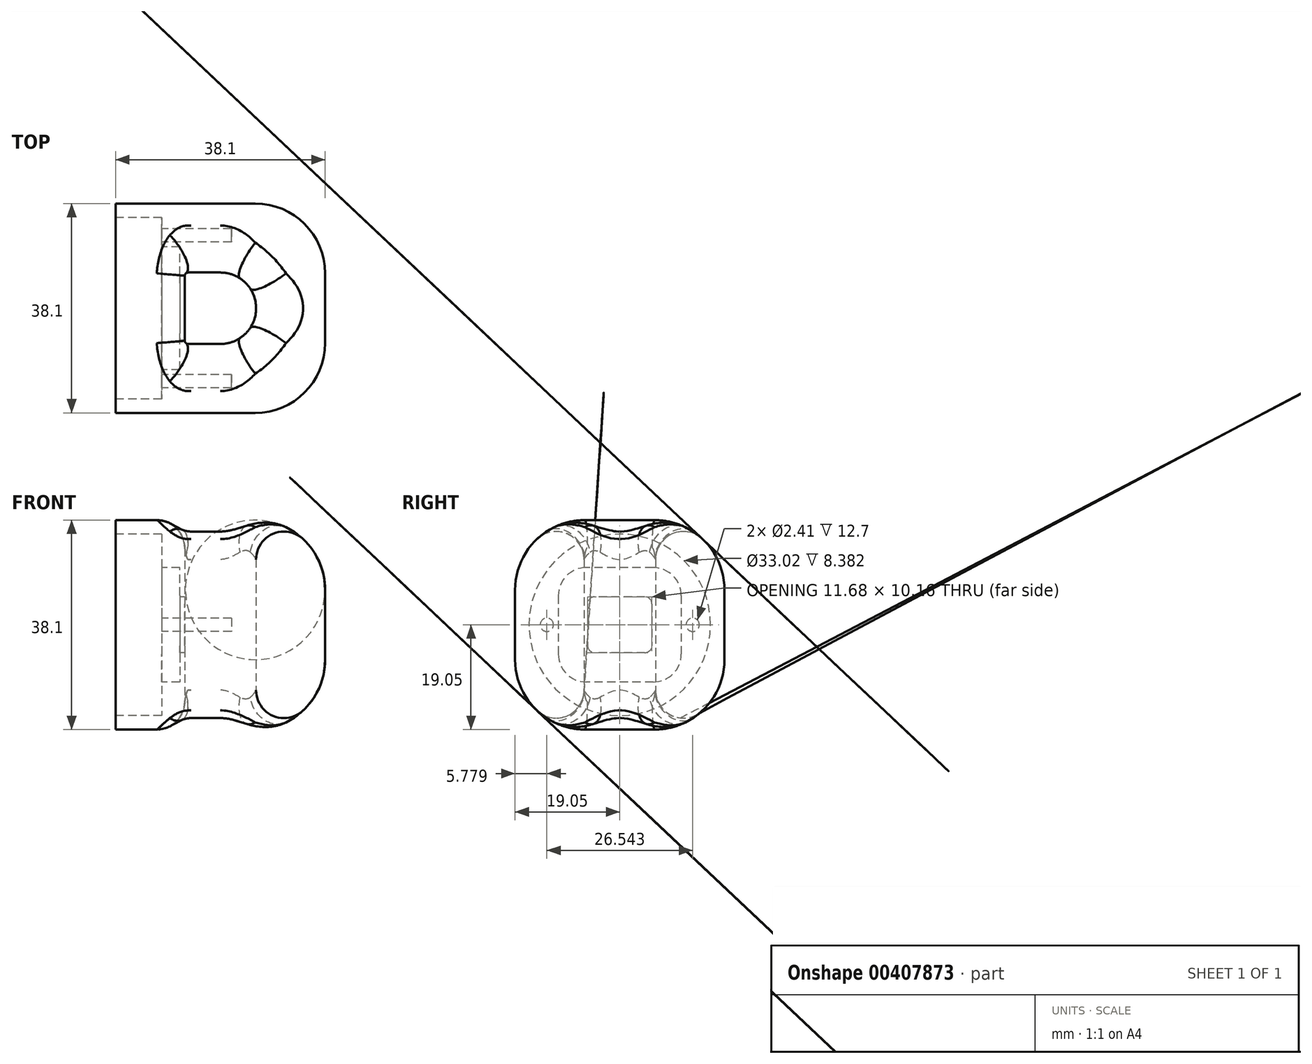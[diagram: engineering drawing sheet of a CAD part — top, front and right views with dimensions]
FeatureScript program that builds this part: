
annotation { "Feature Type Name" : "Feature", "Feature Type Description" : "" }
export const myFeature = defineFeature(function(context is Context, id is Id, definition is map)
    precondition{}
    {
        {
            var Q0;
            Q0=qCreatedBy(makeId("Top.planeOp"),FACE);
            var sketch = newSketch(context, id + "F0", { "sketchPlane" : qUnion([Q0])});
            skLineSegment(sketch, "E0.bottom", {"start": v(19.05, 19.05) * mm, "end": v(-19.05, 19.05) * mm});
            skLineSegment(sketch, "E0.top", {"start": v(19.05, -19.05) * mm, "end": v(-19.05, -19.05) * mm});
            skLineSegment(sketch, "E0.left", {"start": v(19.05, 19.05) * mm, "end": v(19.05, -19.05) * mm});
            skLineSegment(sketch, "E0.right", {"start": v(-19.05, 19.05) * mm, "end": v(-19.05, -19.05) * mm});
            skPoint(sketch, "E0.middle", {"position": v(0, 0) * mm});
            skArc(sketch, "E1", {"start": v(0, -6.5) * mm, "mid": v(6.5, 0) * mm, "end": v(0, 6.5) * mm});
            skLineSegment(sketch, "E2", {"start": v(0, 6.5) * mm, "end": v(-6.5, 6.5) * mm});
            skLineSegment(sketch, "E3", {"start": v(0, -6.5) * mm, "end": v(-6.5, -6.5) * mm});
            skLineSegment(sketch, "E4", {"start": v(-6.5, 0) * mm, "end": v(-6.5, 6.5) * mm});
            skLineSegment(sketch, "E5", {"start": v(-6.5, 0) * mm, "end": v(-6.5, -6.5) * mm});
            skSolve(sketch);
        }
        {
            var Q0;
            Q0 = qSketchRegion(id + "F0", true);
            extrude(context, id + "F1", {"entities" : qUnion([Q0]), "depth" : 38.1 * mm});
        }
        {
            var Q0;
            Q0=makeQuery(id+"F1.opExtrude","SWEPT_FACE",FACE,{"disambiguationData":[OSD([sQuery(id+"F0.wireOp",EDGE,"E0.right")])]});
            var sketch = newSketch(context, id + "F2", { "sketchPlane" : qUnion([Q0])});
            skCircle(sketch, "E6", {"center": v(0, 19.05) * mm, "radius": 16.51 * mm});
            skPoint(sketch, "E6.centerSnap0", {"position": v(19.05, 19.05) * mm});
            skSolve(sketch);
        }
        {
            var Q0;
            Q0 = qSketchRegion(id + "F2", true);
            extrude(context, id + "F3", {"entities" : qUnion([Q0]), "operationType" : NewBodyOperationType.REMOVE, "oppositeDirection" : true, "depth" : 8.38 * mm});
        }
        {
            var Q0;
            Q0=makeQuery(id+"F3.boolean.opBoolean","COPY",FACE,{"derivedFrom":makeQuery(id+"F3.opExtrude","CAP_FACE",FACE,{"disambiguationData":[OSD([sQuery(id+"F2.wireOp",EDGE,"E6")])],"isStart":false})});
            var sketch = newSketch(context, id + "F4", { "sketchPlane" : qUnion([Q0])});
            skCircle(sketch, "E7", {"center": v(-13.27, 19.05) * mm, "radius": 1.2 * mm});
            skCircle(sketch, "E8", {"center": v(13.27, 19.05) * mm, "radius": 1.2 * mm});
            skPoint(sketch, "E9.center.orphan", {"position": v(0, 19.05) * mm});
            skSolve(sketch);
        }
        {
            var Q0;
            Q0 = qSketchRegion(id + "F4", true);
            extrude(context, id + "F5", {"entities" : qUnion([Q0]), "operationType" : NewBodyOperationType.REMOVE, "oppositeDirection" : true, "depth" : 12.7 * mm});
        }
        {
            var Q0;
            Q0=makeQuery(id+"F3.boolean.opBoolean","COPY",FACE,{"derivedFrom":makeQuery(id+"F3.opExtrude","CAP_FACE",FACE,{"disambiguationData":[OSD([sQuery(id+"F2.wireOp",EDGE,"E6")])],"isStart":false})});
            var sketch = newSketch(context, id + "F6", { "sketchPlane" : qUnion([Q0])});
            skLineSegment(sketch, "E10", {"start": v(-11.18, 29.46) * mm, "end": v(11.18, 29.46) * mm});
            skLineSegment(sketch, "E11", {"start": v(-11.18, 8.64) * mm, "end": v(11.18, 8.64) * mm});
            skLineSegment(sketch, "E12", {"start": v(-11.18, 29.46) * mm, "end": v(-11.18, 8.64) * mm});
            skLineSegment(sketch, "E13", {"start": v(11.18, 29.46) * mm, "end": v(11.18, 8.64) * mm});
            skPoint(sketch, "E14.center.orphan", {"position": v(0, 19.05) * mm});
            skSolve(sketch);
        }
        {
            var Q0;
            Q0 = qSketchRegion(id + "F6", true);
            extrude(context, id + "F7", {"entities" : qUnion([Q0]), "operationType" : NewBodyOperationType.REMOVE, "oppositeDirection" : true, "depth" : 3.3 * mm});
        }
        {
            var Q0;
            Q0=makeQuery(id+"F7.boolean.opBoolean","COPY",EDGE,{"derivedFrom":makeQuery(id+"F7.opExtrude","SWEPT_EDGE",EDGE,{"disambiguationData":[OSD([sQuery(id+"F6.wireOp",EDGE,"E10"),sQuery(id+"F6.wireOp",EDGE,"E12")])]})});
            var Q1;
            Q1=makeQuery(id+"F7.boolean.opBoolean","COPY",EDGE,{"derivedFrom":makeQuery(id+"F7.opExtrude","SWEPT_EDGE",EDGE,{"disambiguationData":[OSD([sQuery(id+"F6.wireOp",EDGE,"E11"),sQuery(id+"F6.wireOp",EDGE,"E12")])]})});
            var Q2;
            Q2=makeQuery(id+"F7.boolean.opBoolean","COPY",EDGE,{"derivedFrom":makeQuery(id+"F7.opExtrude","SWEPT_EDGE",EDGE,{"disambiguationData":[OSD([sQuery(id+"F6.wireOp",EDGE,"E11"),sQuery(id+"F6.wireOp",EDGE,"E13")])]})});
            var Q3;
            Q3=makeQuery(id+"F7.boolean.opBoolean","COPY",EDGE,{"derivedFrom":makeQuery(id+"F7.opExtrude","SWEPT_EDGE",EDGE,{"disambiguationData":[OSD([sQuery(id+"F6.wireOp",EDGE,"E10"),sQuery(id+"F6.wireOp",EDGE,"E13")])]})});
            fillet(context, id + "F8", {"entities" : qUnion([Q0, Q1, Q2, Q3]), "radius" : 5.08 * mm, "tangentPropagation" : true, "allowEdgeOverflow" : false});
        }
        {
            var Q0;
            Q0=makeQuery(id+"F7.boolean.opBoolean","COPY",FACE,{"derivedFrom":makeQuery(id+"F7.opExtrude","CAP_FACE",FACE,{"disambiguationData":[OSD([sQuery(id+"F6.wireOp",EDGE,"E10"),sQuery(id+"F6.wireOp",EDGE,"E11"),sQuery(id+"F6.wireOp",EDGE,"E12"),sQuery(id+"F6.wireOp",EDGE,"E13")])],"isStart":false})});
            var sketch = newSketch(context, id + "F9", { "sketchPlane" : qUnion([Q0])});
            skPoint(sketch, "E15.centerSnap0", {"position": v(-11.18, 19.05) * mm});
            skLineSegment(sketch, "E16", {"start": v(-5.84, 24.13) * mm, "end": v(5.84, 24.13) * mm});
            skLineSegment(sketch, "E17", {"start": v(-5.84, 13.97) * mm, "end": v(5.84, 13.97) * mm});
            skLineSegment(sketch, "E18", {"start": v(5.84, 24.13) * mm, "end": v(5.84, 13.97) * mm});
            skLineSegment(sketch, "E19", {"start": v(-5.84, 24.13) * mm, "end": v(-5.84, 13.97) * mm});
            skPoint(sketch, "E19.startSnap0", {"position": v(-9.69, 27.98) * mm});
            skPoint(sketch, "E20.orphan", {"position": v(-5.84, 27.98) * mm});
            skPoint(sketch, "E15.center.orphan", {"position": v(0, 19.05) * mm});
            skSolve(sketch);
        }
        {
            var Q0;
            Q0 = qSketchRegion(id + "F9", true);
            extrude(context, id + "F10", {"entities" : qUnion([Q0]), "operationType" : NewBodyOperationType.REMOVE, "oppositeDirection" : true, "depth" : 3.3 * mm});
        }
        {
            var Q0;
            Q0=makeQuery(id+"F10.boolean.opBoolean","COPY",EDGE,{"derivedFrom":makeQuery(id+"F10.opExtrude","SWEPT_EDGE",EDGE,{"disambiguationData":[OSD([sQuery(id+"F9.wireOp",EDGE,"E16"),sQuery(id+"F9.wireOp",EDGE,"E18")])]})});
            var Q1;
            Q1=makeQuery(id+"F10.boolean.opBoolean","COPY",EDGE,{"derivedFrom":makeQuery(id+"F10.opExtrude","SWEPT_EDGE",EDGE,{"disambiguationData":[OSD([sQuery(id+"F9.wireOp",EDGE,"E16"),sQuery(id+"F9.wireOp",EDGE,"E19")])]})});
            var Q2;
            Q2=makeQuery(id+"F10.boolean.opBoolean","COPY",EDGE,{"derivedFrom":makeQuery(id+"F10.opExtrude","SWEPT_EDGE",EDGE,{"disambiguationData":[OSD([sQuery(id+"F9.wireOp",EDGE,"E17"),sQuery(id+"F9.wireOp",EDGE,"E18")])]})});
            var Q3;
            Q3=makeQuery(id+"F10.boolean.opBoolean","COPY",EDGE,{"derivedFrom":makeQuery(id+"F10.opExtrude","SWEPT_EDGE",EDGE,{"disambiguationData":[OSD([sQuery(id+"F9.wireOp",EDGE,"E17"),sQuery(id+"F9.wireOp",EDGE,"E19")])]})});
            fillet(context, id + "F11", {"entities" : qUnion([Q0, Q1, Q2, Q3]), "radius" : 1.27 * mm, "tangentPropagation" : true, "allowEdgeOverflow" : false});
        }
        {
            var Q0;
            Q0=makeQuery(id+"F1.opExtrude","SWEPT_EDGE",EDGE,{"disambiguationData":[OSD([sQuery(id+"F0.wireOp",EDGE,"E0.bottom"),sQuery(id+"F0.wireOp",EDGE,"E0.left")])]});
            var Q1;
            Q1=makeQuery(id+"F1.opExtrude","SWEPT_EDGE",EDGE,{"disambiguationData":[OSD([sQuery(id+"F0.wireOp",EDGE,"E0.top"),sQuery(id+"F0.wireOp",EDGE,"E0.left")])]});
            var Q2;
            Q2=makeQuery(id+"F1.opExtrude","CAP_EDGE",EDGE,{"disambiguationData":[OSD([sQuery(id+"F0.wireOp",EDGE,"E0.top")])],"isStart":false});
            var Q3;
            Q3=makeQuery(id+"F1.opExtrude","CAP_EDGE",EDGE,{"disambiguationData":[OSD([sQuery(id+"F0.wireOp",EDGE,"E0.bottom")])],"isStart":false});
            var Q4;
            Q4=makeQuery(id+"F1.opExtrude","CAP_EDGE",EDGE,{"disambiguationData":[OSD([sQuery(id+"F0.wireOp",EDGE,"E0.bottom")])],"isStart":true});
            var Q5;
            Q5=makeQuery(id+"F1.opExtrude","CAP_EDGE",EDGE,{"disambiguationData":[OSD([sQuery(id+"F0.wireOp",EDGE,"E0.top")])],"isStart":true});
            var Q6;
            Q6=makeQuery(id+"F1.opExtrude","CAP_EDGE",EDGE,{"disambiguationData":[OSD([sQuery(id+"F0.wireOp",EDGE,"E0.left")])],"isStart":true});
            var Q7;
            Q7=makeQuery(id+"F1.opExtrude","CAP_EDGE",EDGE,{"disambiguationData":[OSD([sQuery(id+"F0.wireOp",EDGE,"E0.left")])],"isStart":false});
            fillet(context, id + "F12", {"entities" : qUnion([Q0, Q1, Q2, Q3, Q4, Q5, Q6, Q7]), "radius" : 12.7 * mm, "tangentPropagation" : true, "allowEdgeOverflow" : false});
        }
        {
            var Q0;
            Q0=makeQuery(id+"F1.opExtrude","SWEPT_EDGE",EDGE,{"disambiguationData":[OSD([sQuery(id+"F0.wireOp",EDGE,"E2"),sQuery(id+"F0.wireOp",EDGE,"E4")])]});
            var Q1;
            Q1=makeQuery(id+"F1.opExtrude","SWEPT_EDGE",EDGE,{"disambiguationData":[OSD([sQuery(id+"F0.wireOp",EDGE,"E3"),sQuery(id+"F0.wireOp",EDGE,"E5")])]});
            fillet(context, id + "F13", {"entities" : qUnion([Q0, Q1]), "radius" : 0.64 * mm, "tangentPropagation" : true, "allowEdgeOverflow" : false});
        }
        {
            var Q0;
            Q0=makeQuery(id+"F1.opExtrude","CAP_EDGE",EDGE,{"disambiguationData":[OSD([sQuery(id+"F0.wireOp",EDGE,"E4"),sQuery(id+"F0.wireOp",EDGE,"E5")])],"isStart":false});
            var Q1;
            Q1=makeQuery(id+"F1.opExtrude","CAP_EDGE",EDGE,{"disambiguationData":[OSD([sQuery(id+"F0.wireOp",EDGE,"E4"),sQuery(id+"F0.wireOp",EDGE,"E5")])],"isStart":true});
            fillet(context, id + "F14", {"entities" : qUnion([Q0, Q1]), "radius" : 5.08 * mm, "tangentPropagation" : true, "allowEdgeOverflow" : false});
        }
    });
